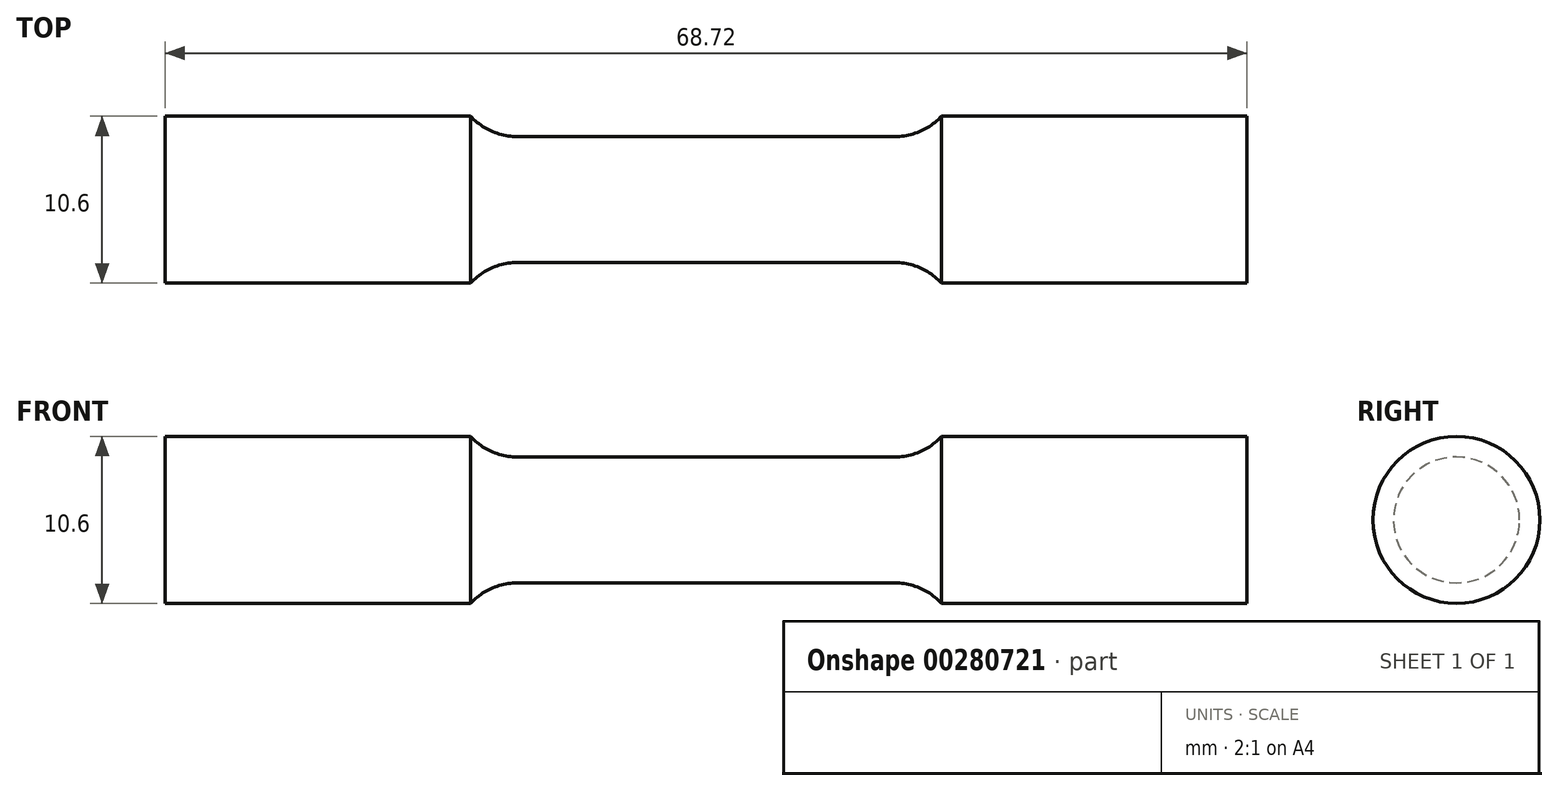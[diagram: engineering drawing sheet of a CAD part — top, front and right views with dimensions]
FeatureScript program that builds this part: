
annotation { "Feature Type Name" : "Feature", "Feature Type Description" : "" }
export const myFeature = defineFeature(function(context is Context, id is Id, definition is map)
    precondition{}
    {
        {
            var Q0;
            Q0=qCreatedBy(makeId("Front.planeOp"),FACE);
            var sketch = newSketch(context, id + "F0", { "sketchPlane" : qUnion([Q0])});
            skLineSegment(sketch, "E0", {"start": v(0, 4) * mm, "end": v(12, 4) * mm});
            skArc(sketch, "E1", {"start": v(12, 4) * mm, "mid": v(13.61, 4.34) * mm, "end": v(14.95, 5.3) * mm});
            skLineSegment(sketch, "E2", {"start": v(14.95, 5.3) * mm, "end": v(34.36, 5.3) * mm});
            skLineSegment(sketch, "E3", {"start": v(34.36, 5.3) * mm, "end": v(34.36, 0) * mm});
            skLineSegment(sketch, "E4.MirrorCS", {"start": v(0, 4) * mm, "end": v(-12, 4) * mm});
            skLineSegment(sketch, "E5.MirrorCS", {"start": v(-34.36, 5.3) * mm, "end": v(-34.36, 0) * mm});
            skLineSegment(sketch, "E6.MirrorCS", {"start": v(-14.95, 5.3) * mm, "end": v(-34.36, 5.3) * mm});
            skArc(sketch, "E7.MirrorCS", {"start": v(-12, 4) * mm, "mid": v(-13.61, 4.34) * mm, "end": v(-14.95, 5.3) * mm});
            skLineSegment(sketch, "E8", {"start": v(-34.36, 0) * mm, "end": v(34.36, 0) * mm});
            skSolve(sketch);
        }
        {
            var Q0;
            Q0 = qSketchRegion(id + "F0", true);
            var Q1;
            Q1=sQuery(id+"F0.wireOp",EDGE,"E8");
            revolve(context, id + "F1", {"entities" : qUnion([Q0]), "axis" : qUnion([Q1]), "revolveType" : RevolveType.FULL});
        }
    });
